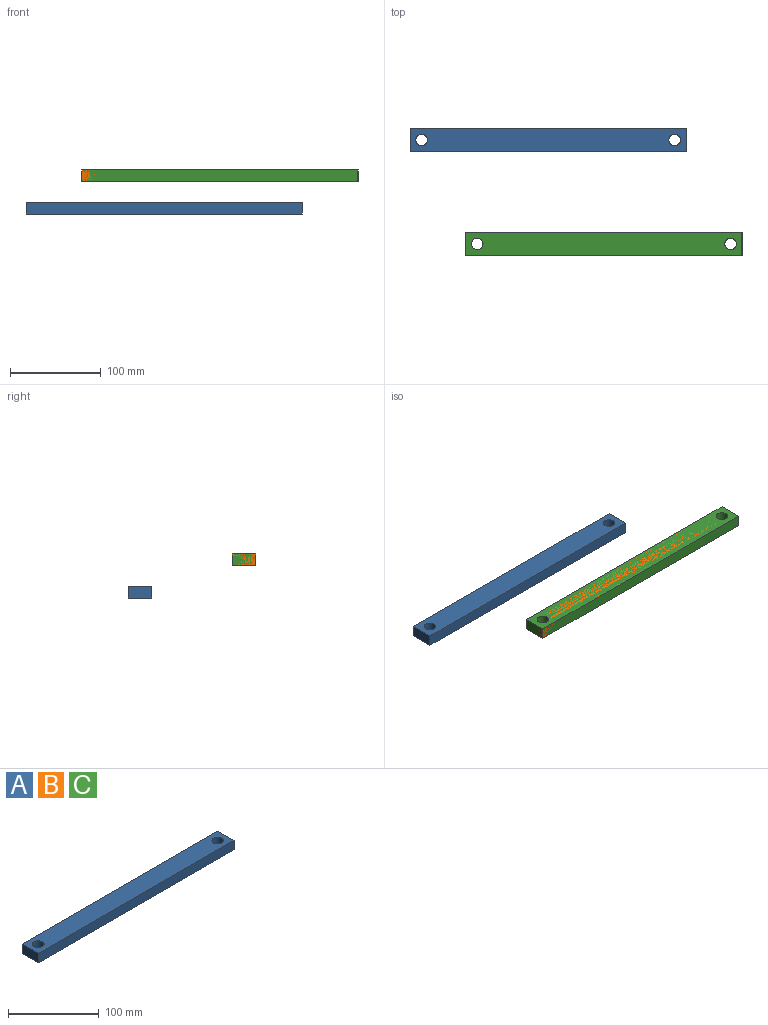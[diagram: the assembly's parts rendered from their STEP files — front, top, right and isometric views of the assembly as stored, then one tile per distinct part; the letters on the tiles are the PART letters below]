
ASSEMBLY  parts=3 mates=1
PART A: 8 faces, bbox 304.8x25.4x12.7 mm
  f0: plane 304.8x12.7mm, normal (0,1,0), area 3871mm2, adj f1,f5,f6,f7
  f1: plane 25.4x12.7mm, normal (-1,0,0), area 322.6mm2, adj f0,f2,f6,f7
  f2: plane 304.8x12.7mm, normal (0,-1,0), area 3871mm2, adj f1,f5,f6,f7
  f3: cylinder r=6.35mm len=12.7mm, axis (0,0,-1), area 506.7mm2, adj f6,f7
  f4: cylinder r=6.35mm len=12.7mm, axis (0,0,-1), area 506.7mm2, adj f6,f7
  f5: plane 25.4x12.7mm, normal (1,0,0), area 322.6mm2, adj f0,f2,f6,f7
  f6: plane 304.8x25.4mm, normal (0,0,1), area 7488.6mm2, adj f0,f1,f2,f3,f4,f5
  f7: plane 304.8x25.4mm, normal (0,0,-1), area 7488.6mm2, adj f0,f1,f2,f3,f4,f5
PART B: same geometry as A
PART C: same geometry as A
PLACE A t=(-186.7,148.44,3.79)mm
PLACE B t=(-125.2,33.7,39.69)mm
PLACE C t=(-125.2,33.7,39.69)mm
MATE ball B.f4 <-> C.f4  axis (0,0,-1) through (166.9,46.4,46.04)mm
